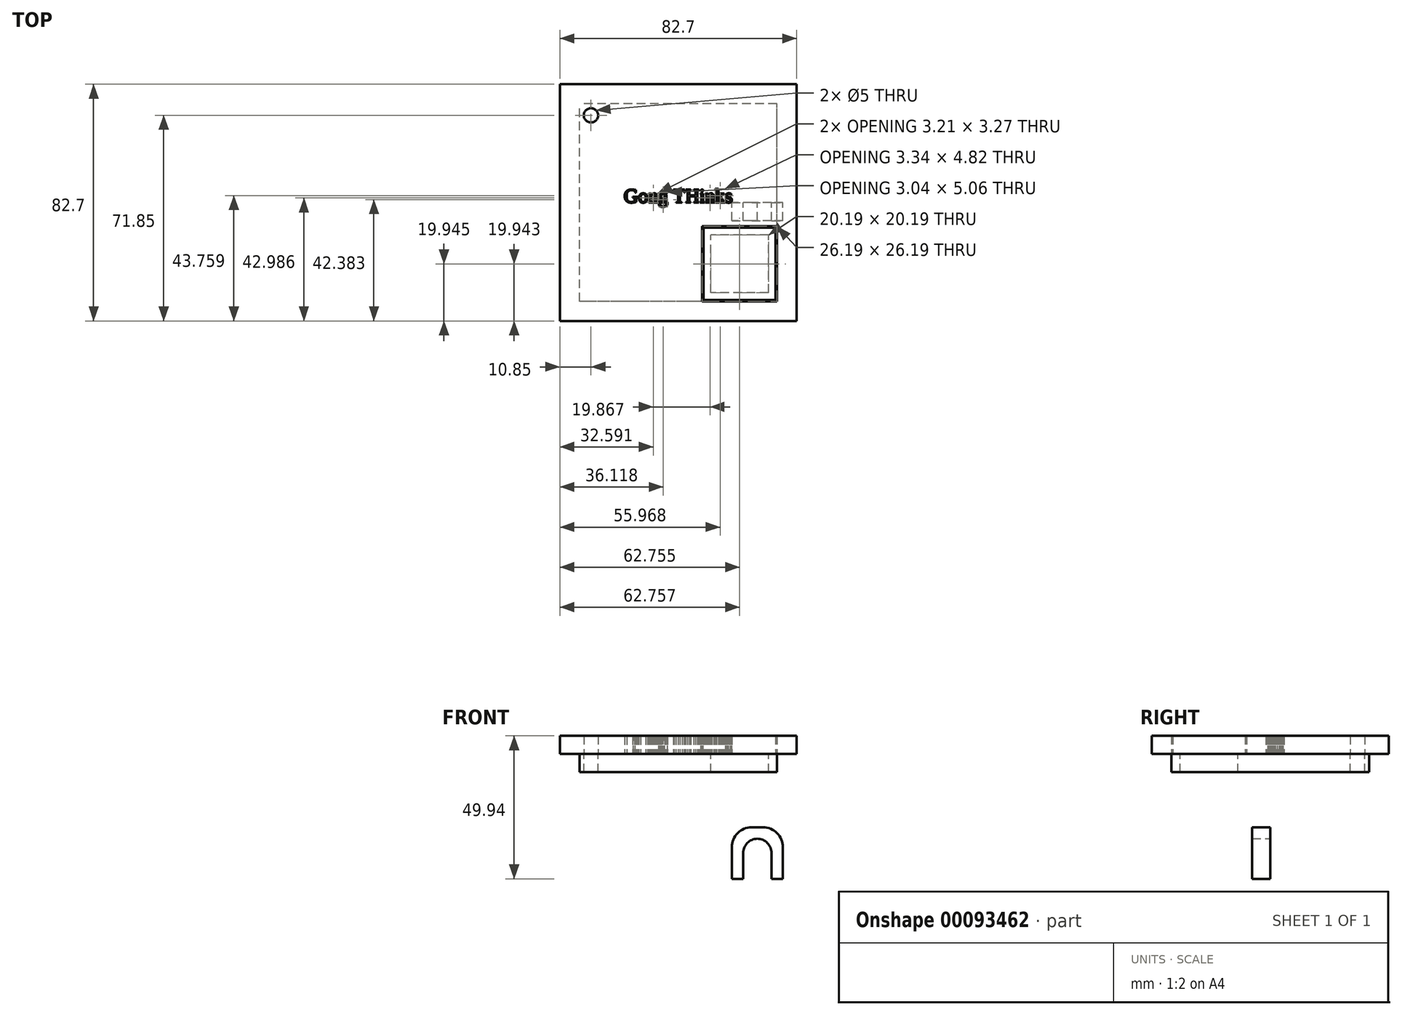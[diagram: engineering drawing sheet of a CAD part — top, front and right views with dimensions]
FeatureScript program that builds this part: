
annotation { "Feature Type Name" : "Feature", "Feature Type Description" : "" }
export const myFeature = defineFeature(function(context is Context, id is Id, definition is map)
    precondition{}
    {
        {
            var Q0;
            Q0=qCreatedBy(makeId("Top.planeOp"),FACE);
            var sketch = newSketch(context, id + "F0", { "sketchPlane" : qUnion([Q0])});
            skPoint(sketch, "E0.middle", {"position": v(0, 0) * mm});
            skLineSegment(sketch, "E1.bottom", {"start": v(41.35, -41.35) * mm, "end": v(-41.35, -41.35) * mm});
            skLineSegment(sketch, "E1.top", {"start": v(41.35, 41.35) * mm, "end": v(-41.35, 41.35) * mm});
            skLineSegment(sketch, "E1.left", {"start": v(41.35, -41.35) * mm, "end": v(41.35, 41.35) * mm});
            skLineSegment(sketch, "E1.right", {"start": v(-41.35, -41.35) * mm, "end": v(-41.35, 41.35) * mm});
            skLineSegment(sketch, "E2.bottom", {"start": v(34.5, -34.5) * mm, "end": v(8.31, -34.5) * mm});
            skLineSegment(sketch, "E2.top", {"start": v(34.5, -8.3) * mm, "end": v(8.31, -8.3) * mm});
            skLineSegment(sketch, "E2.left", {"start": v(34.5, -34.5) * mm, "end": v(34.5, -8.3) * mm});
            skLineSegment(sketch, "E2.right", {"start": v(8.31, -34.5) * mm, "end": v(8.31, -8.3) * mm});
            skPoint(sketch, "E2.middle", {"position": v(21.4, -21.4) * mm});
            skLineSegment(sketch, "E3.bottom", {"start": v(34, -34) * mm, "end": v(8.8, -34) * mm});
            skLineSegment(sketch, "E3.top", {"start": v(34, -8.8) * mm, "end": v(8.81, -8.8) * mm});
            skLineSegment(sketch, "E3.left", {"start": v(34, -34) * mm, "end": v(34, -8.8) * mm});
            skLineSegment(sketch, "E3.right", {"start": v(8.8, -34) * mm, "end": v(8.81, -8.8) * mm});
            skText(sketch, "E4", { "text": "Gong THinks", "fontName": "Tinos-Regular.ttf"});
            const initialGuessF0  = {"E4": [-0.01901, 0, 1, 0, 0.005]};
            skSetInitialGuess(sketch, initialGuessF0);
            skSolve(sketch);
        }
        {
            var Q0;
            Q0=qCreatedBy(makeId("Top.planeOp"),FACE);
            var sketch = newSketch(context, id + "F1", { "sketchPlane" : qUnion([Q0])});
            skLineSegment(sketch, "E5.bottom", {"start": v(34.5, -34.5) * mm, "end": v(-34.5, -34.5) * mm});
            skLineSegment(sketch, "E5.top", {"start": v(34.5, 34.5) * mm, "end": v(-34.5, 34.5) * mm});
            skLineSegment(sketch, "E5.left", {"start": v(34.5, -34.5) * mm, "end": v(34.5, 34.5) * mm});
            skLineSegment(sketch, "E5.right", {"start": v(-34.5, -34.5) * mm, "end": v(-34.5, 34.5) * mm});
            skPoint(sketch, "E5.middle", {"position": v(0, 0) * mm});
            skLineSegment(sketch, "E6.bottom", {"start": v(31.5, -31.5) * mm, "end": v(11.31, -31.5) * mm});
            skLineSegment(sketch, "E6.top", {"start": v(31.5, -11.31) * mm, "end": v(11.31, -11.31) * mm});
            skLineSegment(sketch, "E6.left", {"start": v(31.5, -31.5) * mm, "end": v(31.5, -11.31) * mm});
            skLineSegment(sketch, "E6.right", {"start": v(11.31, -31.5) * mm, "end": v(11.31, -11.31) * mm});
            skPoint(sketch, "E6.middle", {"position": v(21.4, -21.4) * mm});
            skCircle(sketch, "E7", {"center": v(-30.5, 30.5) * mm, "radius": 2.5 * mm});
            skSolve(sketch);
        }
        {
            var Q0;
            Q0 = qSketchRegion(id + "F1", true);
            extrude(context, id + "F2", {"entities" : qUnion([Q0]), "oppositeDirection" : true, "depth" : 6.35 * mm});
        }
        {
            var Q0;
            Q0=makeQuery(id+"F0.imprint","IMPRINT",FACE,{"disambiguationData":[TD([[makeQuery(id+"F0.imprint","IMPRINT",EDGE,{"derivedFrom":sQuery(id+"F0.wireOp",EDGE,"E4.sketch_text.stroke-226")}),-1.0]])]});
            var Q1;
            Q1=makeQuery(id+"F0.imprint","IMPRINT",FACE,{"disambiguationData":[TD([[makeQuery(id+"F0.imprint","IMPRINT",EDGE,{"derivedFrom":sQuery(id+"F0.wireOp",EDGE,"E4.sketch_text.stroke-200")}),-1.0]])]});
            var Q2;
            Q2=makeQuery(id+"F0.imprint","IMPRINT",FACE,{"disambiguationData":[TD([[makeQuery(id+"F0.imprint","IMPRINT",EDGE,{"derivedFrom":sQuery(id+"F0.wireOp",EDGE,"E4.sketch_text.stroke-175")}),-1.0]])]});
            var Q3;
            Q3=makeQuery(id+"F0.imprint","IMPRINT",FACE,{"disambiguationData":[TD([[makeQuery(id+"F0.imprint","IMPRINT",EDGE,{"derivedFrom":sQuery(id+"F0.wireOp",EDGE,"E4.sketch_text.stroke-165")}),-1.0]])]});
            var Q4;
            Q4=makeQuery(id+"F0.imprint","IMPRINT",FACE,{"disambiguationData":[TD([[makeQuery(id+"F0.imprint","IMPRINT",EDGE,{"derivedFrom":sQuery(id+"F0.wireOp",EDGE,"E4.sketch_text.stroke-129")}),-1.0]])]});
            var Q5;
            Q5=makeQuery(id+"F0.imprint","IMPRINT",FACE,{"disambiguationData":[TD([[makeQuery(id+"F0.imprint","IMPRINT",EDGE,{"derivedFrom":sQuery(id+"F0.wireOp",EDGE,"E4.sketch_text.stroke-110")}),-1.0]])]});
            var Q6;
            Q6=makeQuery(id+"F0.imprint","IMPRINT",FACE,{"disambiguationData":[TD([[makeQuery(id+"F0.imprint","IMPRINT",EDGE,{"derivedFrom":sQuery(id+"F0.wireOp",EDGE,"E4.sketch_text.stroke-65")}),-1.0]])]});
            var Q7;
            Q7=makeQuery(id+"F0.imprint","IMPRINT",FACE,{"disambiguationData":[TD([[makeQuery(id+"F0.imprint","IMPRINT",EDGE,{"derivedFrom":sQuery(id+"F0.wireOp",EDGE,"E4.sketch_text.stroke-40")}),-1.0]])]});
            var Q8;
            Q8=makeQuery(id+"F0.imprint","IMPRINT",FACE,{"disambiguationData":[TD([[makeQuery(id+"F0.imprint","IMPRINT",EDGE,{"derivedFrom":sQuery(id+"F0.wireOp",EDGE,"E4.sketch_text.stroke-25")}),-1.0]])]});
            var Q9;
            Q9=makeQuery(id+"F0.imprint","IMPRINT",FACE,{"disambiguationData":[TD([[makeQuery(id+"F0.imprint","IMPRINT",EDGE,{"derivedFrom":sQuery(id+"F0.wireOp",EDGE,"E4.sketch_text.stroke-0")}),-1.0]])]});
            extrude(context, id + "F3", {"entities" : qUnion([Q0, Q1, Q2, Q3, Q4, Q5, Q6, Q7, Q8, Q9]), "operationType" : NewBodyOperationType.ADD, "depth" : 6.25 * mm});
        }
        {
            var Q0;
            Q0=qCreatedBy(makeId("Front.planeOp"),FACE);
            var sketch = newSketch(context, id + "F4", { "sketchPlane" : qUnion([Q0])});
            skLineSegment(sketch, "E8.bottom", {"start": v(18.68, -25.6) * mm, "end": v(22.68, -25.6) * mm});
            skLineSegment(sketch, "E8.top", {"start": v(18.68, -43.6) * mm, "end": v(22.68, -43.6) * mm});
            skLineSegment(sketch, "E8.left", {"start": v(18.68, -25.6) * mm, "end": v(18.68, -43.6) * mm});
            skLineSegment(sketch, "E8.right", {"start": v(22.68, -25.6) * mm, "end": v(22.68, -43.6) * mm});
            skLineSegment(sketch, "E9.bottom", {"start": v(32.57, -25.6) * mm, "end": v(36.57, -25.6) * mm});
            skLineSegment(sketch, "E9.top", {"start": v(32.57, -43.6) * mm, "end": v(36.57, -43.6) * mm});
            skLineSegment(sketch, "E9.left", {"start": v(32.57, -25.6) * mm, "end": v(32.57, -43.6) * mm});
            skLineSegment(sketch, "E9.right", {"start": v(36.57, -25.6) * mm, "end": v(36.57, -43.6) * mm});
            skLineSegment(sketch, "E10.bottom", {"start": v(22.68, -25.6) * mm, "end": v(32.57, -25.6) * mm});
            skLineSegment(sketch, "E10.top", {"start": v(22.68, -29.6) * mm, "end": v(32.57, -29.6) * mm});
            skLineSegment(sketch, "E10.left", {"start": v(22.68, -25.6) * mm, "end": v(22.68, -29.6) * mm});
            skLineSegment(sketch, "E10.right", {"start": v(32.57, -25.6) * mm, "end": v(32.57, -29.6) * mm});
            skSolve(sketch);
        }
        {
            var Q0;
            Q0=makeQuery(id+"F4.imprint","IMPRINT",FACE,{"disambiguationData":[TD([[makeQuery(id+"F4.imprint","IMPRINT",EDGE,{"derivedFrom":sQuery(id+"F4.wireOp",EDGE,"E10.bottom")}),-1.0]])]});
            var Q1;
            Q1=makeQuery(id+"F4.imprint","IMPRINT",FACE,{"disambiguationData":[TD([[makeQuery(id+"F4.imprint","IMPRINT",EDGE,{"derivedFrom":sQuery(id+"F4.wireOp",EDGE,"E9.bottom")}),-1.0]])]});
            var Q2;
            Q2=makeQuery(id+"F4.imprint","IMPRINT",FACE,{"disambiguationData":[TD([[makeQuery(id+"F4.imprint","IMPRINT",EDGE,{"derivedFrom":sQuery(id+"F4.wireOp",EDGE,"E8.bottom")}),-1.0]])]});
            extrude(context, id + "F5", {"entities" : qUnion([Q0, Q1, Q2]), "depth" : 6.35 * mm});
        }
        {
            var Q0;
            Q0=makeQuery(id+"F5.opExtrude","SWEPT_EDGE",EDGE,{"disambiguationData":[OSD([sQuery(id+"F4.wireOp",EDGE,"E9.bottom"),sQuery(id+"F4.wireOp",EDGE,"E9.right")])]});
            fillet(context, id + "F6", {"entities" : qUnion([Q0]), "radius" : 7 * mm, "tangentPropagation" : true, "allowEdgeOverflow" : false});
        }
        {
            var Q0;
            Q0=makeQuery(id+"F5.opExtrude","SWEPT_EDGE",EDGE,{"disambiguationData":[OSD([sQuery(id+"F4.wireOp",EDGE,"E8.bottom"),sQuery(id+"F4.wireOp",EDGE,"E8.left")])]});
            fillet(context, id + "F7", {"entities" : qUnion([Q0]), "radius" : 7 * mm, "tangentPropagation" : true, "allowEdgeOverflow" : false});
        }
        {
            var Q0;
            Q0=makeQuery(id+"F5.opExtrude","SWEPT_EDGE",EDGE,{"disambiguationData":[OSD([sQuery(id+"F4.wireOp",EDGE,"E9.left"),sQuery(id+"F4.wireOp",EDGE,"E10.top"),sQuery(id+"F4.wireOp",EDGE,"E10.right")])]});
            fillet(context, id + "F8", {"entities" : qUnion([Q0]), "radius" : 5 * mm, "tangentPropagation" : true, "allowEdgeOverflow" : false});
        }
        {
            var Q0;
            Q0=makeQuery(id+"F5.opExtrude","SWEPT_EDGE",EDGE,{"disambiguationData":[OSD([sQuery(id+"F4.wireOp",EDGE,"E8.right"),sQuery(id+"F4.wireOp",EDGE,"E10.top"),sQuery(id+"F4.wireOp",EDGE,"E10.left")])]});
            fillet(context, id + "F9", {"entities" : qUnion([Q0]), "radius" : 5 * mm, "tangentPropagation" : true, "allowEdgeOverflow" : false});
        }
        {
            var Q0;
            Q0=makeQuery(id+"F0.imprint","IMPRINT",FACE,{"disambiguationData":[TD([[makeQuery(id+"F0.imprint","IMPRINT",EDGE,{"derivedFrom":sQuery(id+"F0.wireOp",EDGE,"E1.bottom")}),-1.0]])]});
            var Q1;
            Q1=makeQuery(id+"F0.imprint","IMPRINT",FACE,{"disambiguationData":[TD([[makeQuery(id+"F0.imprint","IMPRINT",EDGE,{"derivedFrom":sQuery(id+"F0.wireOp",EDGE,"E4.sketch_text.stroke-32")}),1.0]])]});
            var Q2;
            Q2=makeQuery(id+"F0.imprint","IMPRINT",FACE,{"disambiguationData":[TD([[makeQuery(id+"F0.imprint","IMPRINT",EDGE,{"derivedFrom":sQuery(id+"F0.wireOp",EDGE,"E4.sketch_text.stroke-102")}),1.0]])]});
            var Q3;
            Q3=makeQuery(id+"F0.imprint","IMPRINT",FACE,{"disambiguationData":[TD([[makeQuery(id+"F0.imprint","IMPRINT",EDGE,{"derivedFrom":sQuery(id+"F0.wireOp",EDGE,"E4.sketch_text.stroke-93")}),1.0]])]});
            extrude(context, id + "F10", {"entities" : qUnion([Q0, Q1, Q2, Q3]), "depth" : 6.35 * mm});
        }
        {
            var Q0;
            Q0=makeQuery(id+"F1.imprint","IMPRINT",FACE,{"disambiguationData":[TD([[makeQuery(id+"F1.imprint","IMPRINT",EDGE,{"derivedFrom":sQuery(id+"F1.wireOp",EDGE,"E7")}),1.0]])]});
            extrude(context, id + "F11", {"entities" : qUnion([Q0]), "operationType" : NewBodyOperationType.REMOVE, "depth" : 6.35 * mm});
        }
        {
            var Q0;
            Q0=makeQuery(id+"F0.imprint","IMPRINT",FACE,{"disambiguationData":[TD([[makeQuery(id+"F0.imprint","IMPRINT",EDGE,{"derivedFrom":sQuery(id+"F0.wireOp",EDGE,"E3.bottom")}),-1.0]])]});
            extrude(context, id + "F12", {"entities" : qUnion([Q0]), "depth" : 6.35 * mm});
        }
    });
